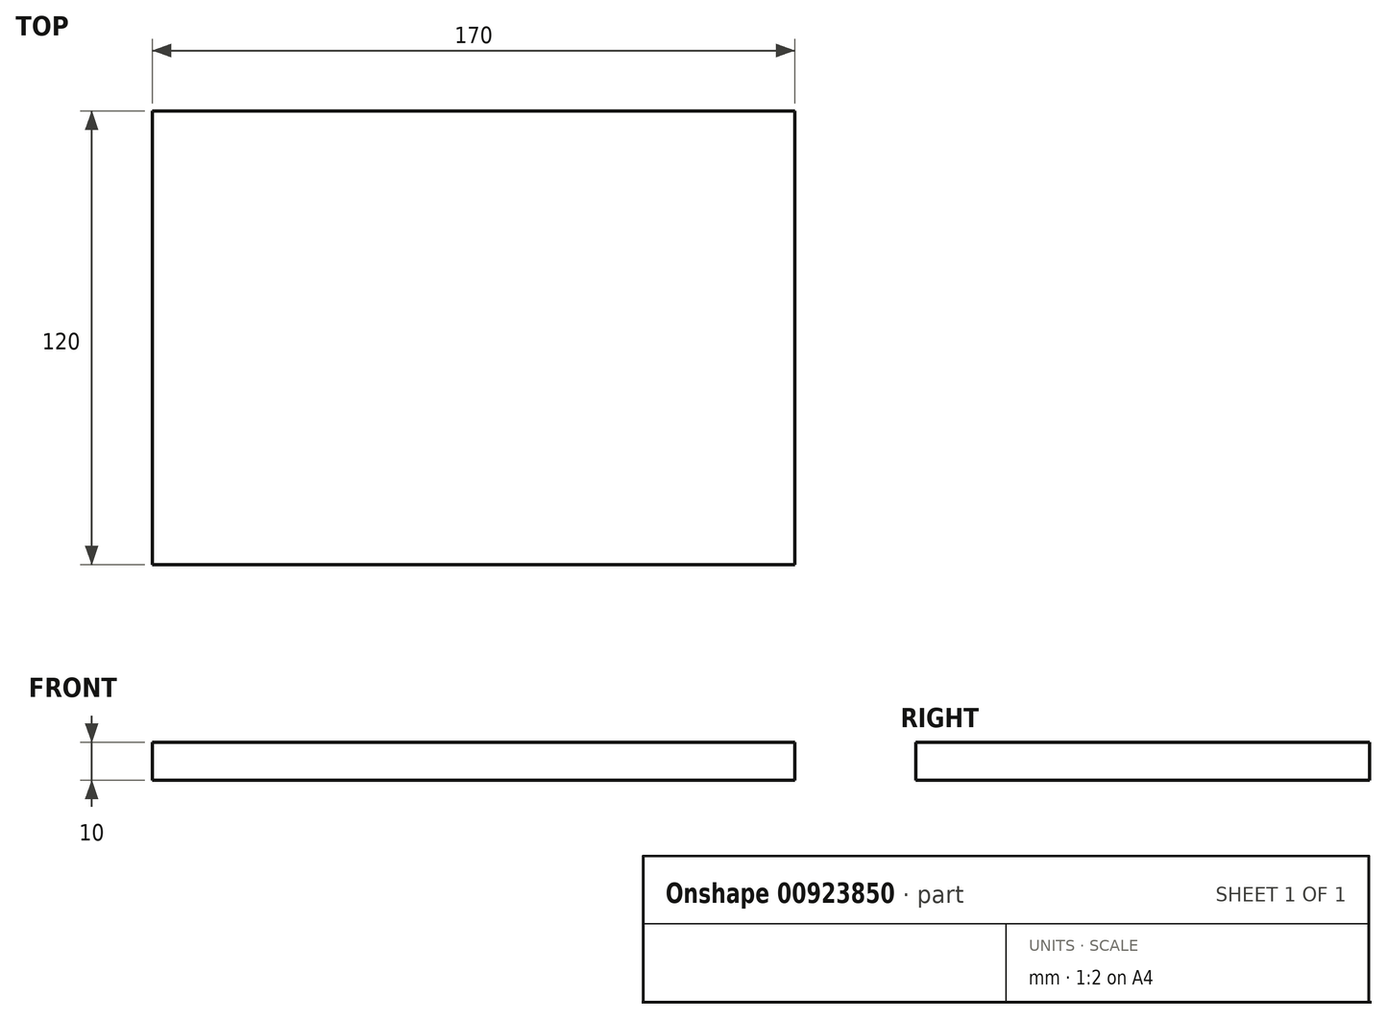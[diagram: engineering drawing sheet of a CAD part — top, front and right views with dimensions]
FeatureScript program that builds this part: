
annotation { "Feature Type Name" : "Feature", "Feature Type Description" : "" }
export const myFeature = defineFeature(function(context is Context, id is Id, definition is map)
    precondition{}
    {
        {
            var Q0;
            Q0=qCreatedBy(makeId("Top.planeOp"),FACE);
            var sketch = newSketch(context, id + "F0", { "sketchPlane" : qUnion([Q0])});
            skLineSegment(sketch, "E0.bottom", {"start": v(85, 60) * mm, "end": v(-85, 60) * mm});
            skLineSegment(sketch, "E0.top", {"start": v(85, -60) * mm, "end": v(-85, -60) * mm});
            skLineSegment(sketch, "E0.left", {"start": v(85, 60) * mm, "end": v(85, -60) * mm});
            skLineSegment(sketch, "E0.right", {"start": v(-85, 60) * mm, "end": v(-85, -60) * mm});
            skPoint(sketch, "E1.middle", {"position": v(0, 0) * mm});
            skSolve(sketch);
        }
        {
            var Q0;
            Q0=makeQuery(id+"F0.imprint","IMPRINT",FACE,{"disambiguationData":[TD([[makeQuery(id+"F0.imprint","IMPRINT",EDGE,{"derivedFrom":sQuery(id+"F0.wireOp",EDGE,"E0.bottom")}),1.0]])]});
            var Q1;
            Q1=makeQuery(id+"F0.imprint","IMPRINT",FACE,{"disambiguationData":[TD([[makeQuery(id+"F0.imprint","IMPRINT",EDGE,{"derivedFrom":sQuery(id+"F0.wireOp",EDGE,"E1.bottom")}),1.0]])]});
            extrude(context, id + "F1", {"entities" : qUnion([Q0, Q1]), "depth" : 10 * mm, "offsetDistance" : 25 * mm});
        }
    });
